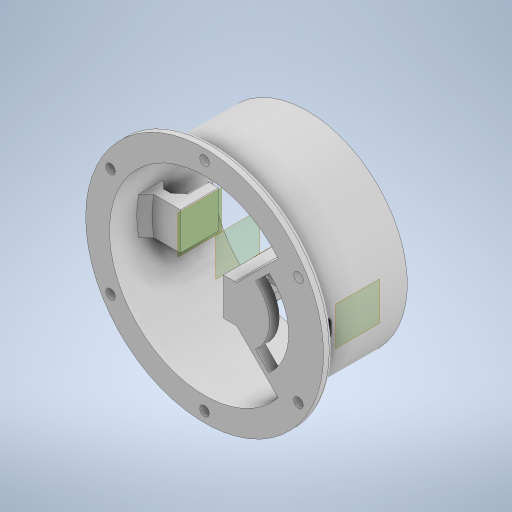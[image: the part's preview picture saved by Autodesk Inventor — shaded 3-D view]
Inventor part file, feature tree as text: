
AUTODESK INVENTOR PART (.ipt)
format: ipt  version: 2023.2 (Build 272271000, 271)  size: 1,011,712 bytes
history: native  units: mm
features: extrude x15, sketch x15, projected_geometry x10, plane x7, other x7, fillet x5, reference x3, chamfer x2
ambient origin geometry x8: Origin, YZ Plane, XZ Plane, XY Plane, X Axis, Y Axis, Z Axis, Center Point
bodies: Solid1 (feature_tree)
feature tree (64):
  plane  "Work Plane1"
  extrude  "Extrusion1"  Depth=100.0mm
  plane  "Work Plane2"
  plane  "Work Plane3"
  plane  "Work Plane4"
  extrude  "Extrusion3"  Depth=50.0mm TaperAngle=0.0deg
  plane  "Work Plane5"
  extrude  "Extrusion7"  Depth=15.0mm TaperAngle=0.0deg
  extrude  "Extrusion8"  TaperAngle=45.0deg  [1 undecoded]
  extrude  "Extrusion9"  Depth=40.0mm
  chamfer  "Chamfer5"  Distance=5.0mm
  extrude  "Extrusion10"  Depth=2.0mm
  fillet  "Fillet1"  Radius=36.860536mm
  extrude  "Extrusion11"  Depth=105.0mm
  plane  "Work Plane6"
  extrude  "Extrusion12"  Depth=2.0mm
  chamfer  "Chamfer7"  [1 undecoded]
  extrude  "Extrusion13"  Depth=2.0mm TaperAngle=360.0deg
  extrude  "Extrusion14"  Depth=2.0mm
  extrude  "Extrusion15"  Depth=10.0mm TaperAngle=0.0deg
  extrude  "Extrusion16"  Depth=2.0mm TaperAngle=45.0deg
  sketch  "Sketch21"  dims[d52=6.525mm d53=105.0mm]
  extrude  "Extrusion17"  Depth=2.0mm
  extrude  "Extrusion18"  Depth=2.0mm
  fillet  "Fillet2"  Radius=36.860536mm
  fillet  "Fillet3"  Radius=6.525mm
  fillet  "Fillet4"  Radius=4.0mm
  plane  "Work Plane7"
  extrude  "Extrusion19"  Depth=2.0mm
  fillet  "Fillet5"  Radius=19.7mm
  sketch  "Sketch3"  dims[d0=15.0mm d1=0.0mm d5=100.0mm]
  reference  "Reference1"
  reference  "Reference2"
  sketch  "Sketch5"  dims[d6=105.0mm d7=50.0mm d8=0.0mm]
  reference  "Reference3"
  projected_geometry  "Projected Loop2"
  sketch  "Sketch10"  dims[d28=9.85mm d30=15.0mm d31=0.0mm]
  projected_geometry  "Projected Loop3"
  projected_geometry  "Projected Loop4"
  sketch  "Sketch11"  dims[d32=15.0mm d33=0.0mm d34=45.0deg]
  projected_geometry  "Projected Loop5"
  sketch  "Sketch12"  dims[d35=45.0deg d36=40.0mm]
  sketch  "Sketch13"  dims[d37=60.0mm]
  projected_geometry  "Projected Loop6"
  sketch  "Sketch14"  dims[d38=4.342145mm]
  sketch  "Sketch15"  dims[d39=9.85mm]
  sketch  "Sketch16"  dims[d40=3.0mm]
  sketch  "Sketch19"  dims[d41=3.0mm d42=5.0mm d43=0.0mm]
  projected_geometry  "Projected Loop7"
  sketch  "Sketch20"  dims[d44=4.0mm d45=2.0mm d46=45.0deg d50=125.0mm d51=36.860536mm]
  projected_geometry  "Projected Loop8"
  sketch  "Sketch22"  dims[d54=5.0mm d55=0.0mm d56=2.0mm]
  projected_geometry  "Projected Loop9"
  sketch  "Sketch23"  dims[d57=5.0mm]
  projected_geometry  "Projected Loop10"
  sketch  "Sketch24"  dims[d58=57.0mm d59=0.0mm d60=0.0mm d61=60.0mm d63=360.0deg d65=5.0mm d66=10.0mm d67=0.0mm d68=4.0mm d69=2.0mm d70=45.0deg d71=105.0mm d72=100.0mm d73=36.860536mm d74=6.525mm d75=4.0mm d76=0.0mm d77=1.0mm d78=19.7mm d79=1.7mm d80=0.0mm d81=0.0mm d82=2.5mm d83=2.5mm d84=2.5mm d85=2.5mm d86=0.0mm d87=0.0mm d88=2.0mm d89=0.0mm d90=2.0mm d91=0.0mm d93=5.0mm d94=10.0mm d95=0.0mm d96=1.0mm d97=2.0mm d98=2.0mm d99=-83.0mm d100=5.0mm d101=10.0mm d102=0.0mm d103=2.0mm]
  projected_geometry  "Projected Loop11"
  other  "<userpath> windows\Documents\Inventor\Robotska_roka\Assembly4.iam"
  other  "Assembly4.iam"
  other  "Servo Motor MG996R  With Attachments:2"
  other  "servoMotorMG996R_7"
  other  "Servo Motor MG996R  With Attachments:1"
  other  "attachmentCircular_1"
  other  "servoMotorMG996R"
note: 2 required parameter values undecoded (feature->parameter linkage not recoverable at this tier; creation-order binding heuristic only, values carry confidence <= 0.55)
